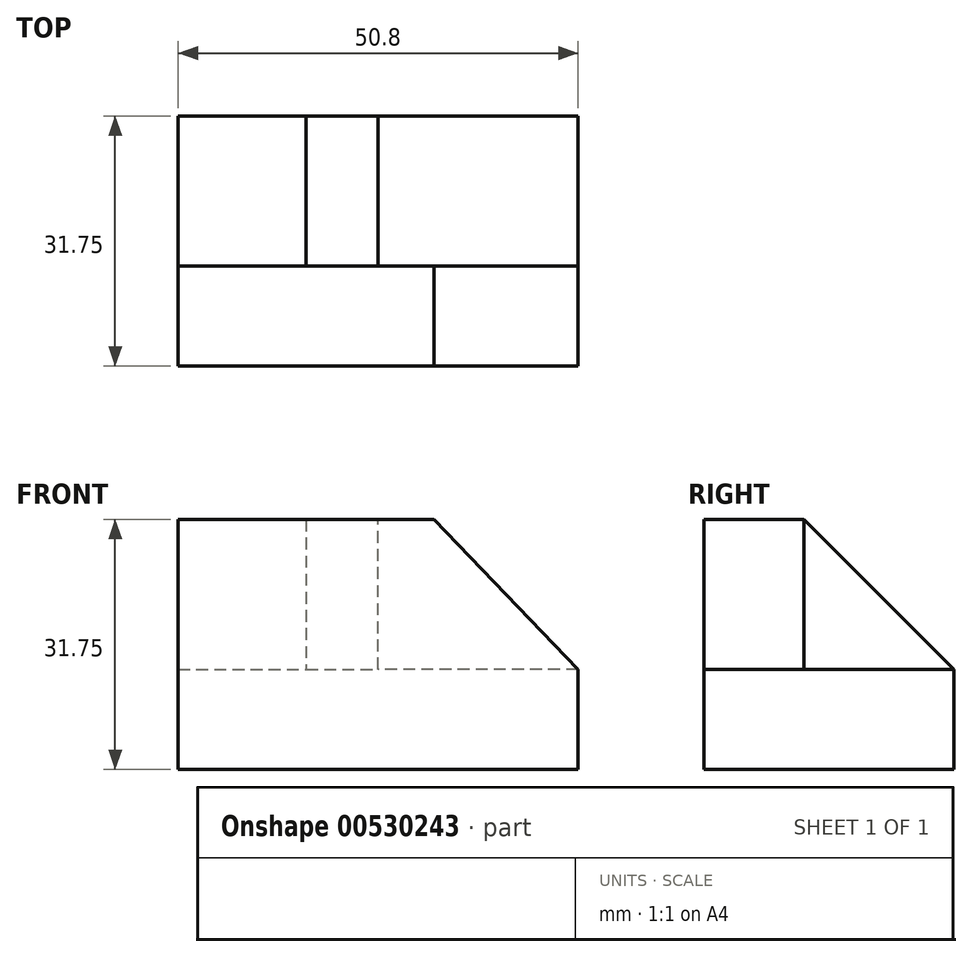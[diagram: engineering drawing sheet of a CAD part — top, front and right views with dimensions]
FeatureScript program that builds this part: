
annotation { "Feature Type Name" : "Feature", "Feature Type Description" : "" }
export const myFeature = defineFeature(function(context is Context, id is Id, definition is map)
    precondition{}
    {
        {
            var Q0;
            Q0=qCreatedBy(makeId("Top.planeOp"),FACE);
            var sketch = newSketch(context, id + "F0", { "sketchPlane" : qUnion([Q0])});
            skLineSegment(sketch, "E0", {"start": v(-32.5, 31.75) * mm, "end": v(-32.5, 0) * mm});
            skLineSegment(sketch, "E1", {"start": v(-32.5, 0) * mm, "end": v(18.3, 0) * mm});
            skLineSegment(sketch, "E2", {"start": v(18.3, 0) * mm, "end": v(18.3, 31.75) * mm});
            skLineSegment(sketch, "E3", {"start": v(18.3, 31.75) * mm, "end": v(-32.5, 31.75) * mm});
            skSolve(sketch);
        }
        {
            var Q0;
            Q0 = qSketchRegion(id + "F0", true);
            extrude(context, id + "F1", {"entities" : qUnion([Q0]), "depth" : 12.7 * mm, "offsetDistance" : 25.4 * mm});
        }
        {
            var Q0;
            Q0=makeQuery(id+"F1.opExtrude","SWEPT_FACE",FACE,{"disambiguationData":[OSD([sQuery(id+"F0.wireOp",EDGE,"E1")])]});
            var sketch = newSketch(context, id + "F2", { "sketchPlane" : qUnion([Q0])});
            skLineSegment(sketch, "E4", {"start": v(-32.5, 12.7) * mm, "end": v(-32.5, 31.75) * mm});
            skLineSegment(sketch, "E5", {"start": v(-32.5, 31.75) * mm, "end": v(18.3, 31.75) * mm});
            skLineSegment(sketch, "E6", {"start": v(18.3, 31.75) * mm, "end": v(18.3, 12.7) * mm});
            skSolve(sketch);
        }
        {
            var Q0;
            Q0=makeQuery(id+"F2.imprint","IMPRINT",FACE,{"disambiguationData":[TD([[makeQuery(id+"F2.imprint","IMPRINT",EDGE,{"derivedFrom":sQuery(id+"F2.wireOp",EDGE,"E4")}),-1.0]])]});
            extrude(context, id + "F3", {"entities" : qUnion([Q0]), "operationType" : NewBodyOperationType.ADD, "oppositeDirection" : true, "depth" : 12.7 * mm, "offsetDistance" : 25.4 * mm});
        }
        {
            var Q0;
            {var subQ0=sQuery(id+"F0.wireOp",EDGE,"E1");Q0=makeQuery(id+"F3.boolean.opBoolean","MERGE",FACE,{"derivedFrom":[makeQuery(id+"F1.opExtrude","SWEPT_FACE",FACE,{"disambiguationData":[OSD([subQ0])]}),makeQuery(id+"F3.opExtrude","CAP_FACE",FACE,{"disambiguationData":[OSD([subQ0,sQuery(id+"F2.wireOp",EDGE,"E4"),sQuery(id+"F2.wireOp",EDGE,"E5"),sQuery(id+"F2.wireOp",EDGE,"E6")])],"isStart":true})]});}
            var sketch = newSketch(context, id + "F4", { "sketchPlane" : qUnion([Q0])});
            skLineSegment(sketch, "E7", {"start": v(0, 31.75) * mm, "end": v(18.3, 12.7) * mm});
            skLineSegment(sketch, "E8", {"start": v(18.3, 12.7) * mm, "end": v(18.3, 31.75) * mm});
            skLineSegment(sketch, "E9", {"start": v(18.3, 31.75) * mm, "end": v(0, 31.75) * mm});
            skSolve(sketch);
        }
        {
            var Q0;
            Q0 = qSketchRegion(id + "F4", true);
            extrude(context, id + "F5", {"entities" : qUnion([Q0]), "operationType" : NewBodyOperationType.REMOVE, "oppositeDirection" : true, "depth" : 25.4 * mm, "offsetDistance" : 25.4 * mm});
        }
        {
            var Q0;
            Q0=makeQuery(id+"F3.opExtrude","CAP_FACE",FACE,{"disambiguationData":[OSD([sQuery(id+"F0.wireOp",EDGE,"E1"),sQuery(id+"F2.wireOp",EDGE,"E4"),sQuery(id+"F2.wireOp",EDGE,"E5"),sQuery(id+"F2.wireOp",EDGE,"E6")])],"isStart":false});
            var sketch = newSketch(context, id + "F6", { "sketchPlane" : qUnion([Q0])});
            skLineSegment(sketch, "E10", {"start": v(7.1, 31.75) * mm, "end": v(16.25, 31.75) * mm});
            skLineSegment(sketch, "E11", {"start": v(16.25, 31.75) * mm, "end": v(16.25, 12.7) * mm});
            skLineSegment(sketch, "E12", {"start": v(16.25, 12.7) * mm, "end": v(7.1, 12.7) * mm});
            skLineSegment(sketch, "E13", {"start": v(7.1, 12.7) * mm, "end": v(7.1, 31.75) * mm});
            skSolve(sketch);
        }
        {
            var Q0;
            Q0=makeQuery(id+"F6.imprint","IMPRINT",FACE,{"disambiguationData":[TD([[makeQuery(id+"F6.imprint","IMPRINT",EDGE,{"derivedFrom":sQuery(id+"F6.wireOp",EDGE,"E10")}),1.0]])]});
            extrude(context, id + "F7", {"entities" : qUnion([Q0]), "operationType" : NewBodyOperationType.ADD, "depth" : 19.05 * mm, "offsetDistance" : 25.4 * mm});
        }
        {
            var Q0;
            Q0=makeQuery(id+"F7.opExtrude","SWEPT_FACE",FACE,{"disambiguationData":[OSD([sQuery(id+"F6.wireOp",EDGE,"E13")])]});
            var sketch = newSketch(context, id + "F8", { "sketchPlane" : qUnion([Q0])});
            skLineSegment(sketch, "E14", {"start": v(12.7, 31.75) * mm, "end": v(31.75, 12.7) * mm});
            skLineSegment(sketch, "E15", {"start": v(31.75, 12.7) * mm, "end": v(31.75, 31.75) * mm});
            skLineSegment(sketch, "E16", {"start": v(31.75, 31.75) * mm, "end": v(12.7, 31.75) * mm});
            skSolve(sketch);
        }
        {
            var Q0;
            Q0=makeQuery(id+"F8.imprint","IMPRINT",FACE,{"disambiguationData":[TD([[makeQuery(id+"F8.imprint","IMPRINT",EDGE,{"derivedFrom":sQuery(id+"F8.wireOp",EDGE,"E14")}),1.0]])]});
            extrude(context, id + "F9", {"entities" : qUnion([Q0]), "operationType" : NewBodyOperationType.REMOVE, "oppositeDirection" : true, "depth" : 25.4 * mm, "offsetDistance" : 25.4 * mm});
        }
    });
